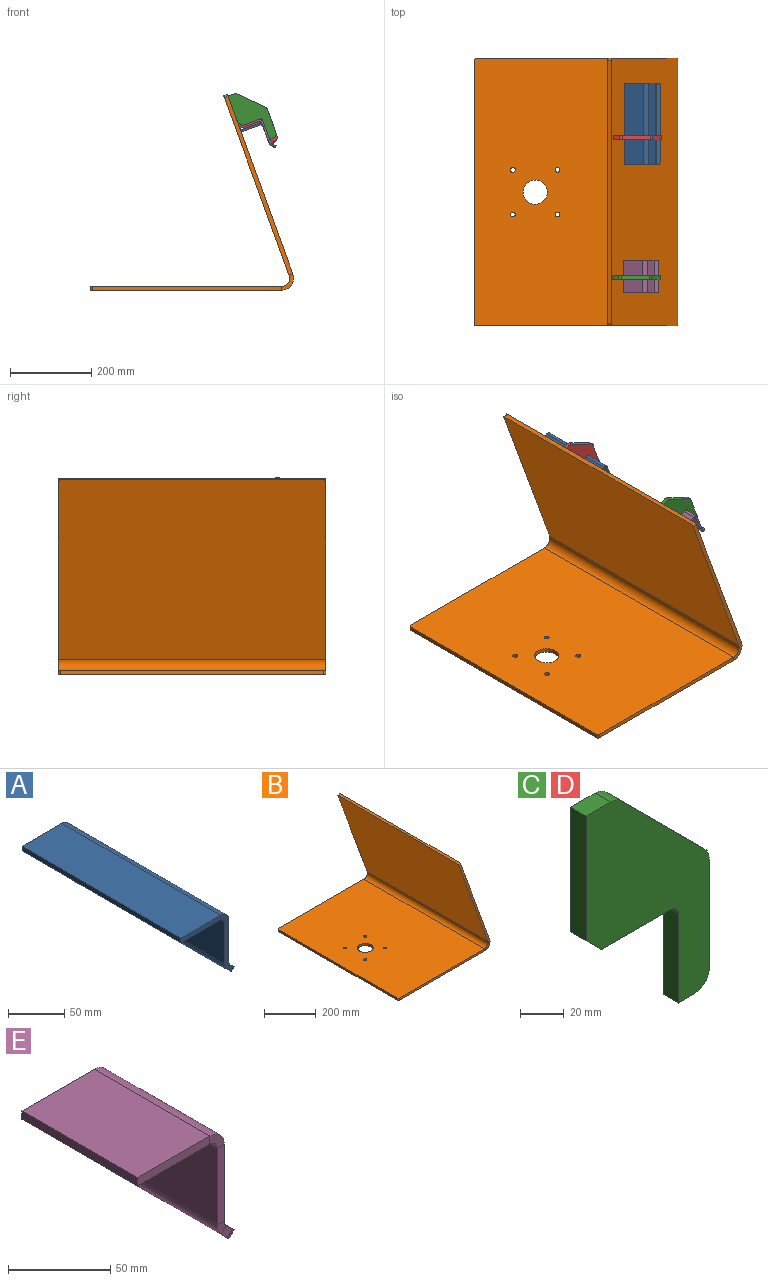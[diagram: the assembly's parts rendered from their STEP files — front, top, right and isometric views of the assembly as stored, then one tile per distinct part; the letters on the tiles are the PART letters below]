
ASSEMBLY  parts=5 mates=6
PART A: 24 faces, bbox 69.1x200x70.6 mm
  f0: plane 50x5mm, normal (0,1,0), area 250mm2, adj f2,f3,f4,f21
  f1: plane 50x5mm, normal (0,-1,0), area 250mm2, adj f2,f3,f4,f20
  f2: plane 200x5mm, normal (-1,0,0), area 1000mm2, adj f0,f1,f3,f4
  f3: plane 200x50mm, normal (0,0,-1), area 10000mm2, adj f0,f1,f2,f23
  f4: plane 200x50mm, normal (0,0,1), area 10000mm2, adj f0,f1,f2,f22
  f5: plane 45.86x5mm, normal (0,1,0), area 229.3mm2, adj f7,f8,f17,f21
  f6: plane 45.86x5mm, normal (0,-1,0), area 229.3mm2, adj f7,f8,f16,f20
  f7: plane 200x45.86mm, normal (-1,0,0), area 9171.6mm2, adj f5,f6,f18,f23
  f8: plane 200x45.86mm, normal (1,0,0), area 9171.6mm2, adj f5,f6,f19,f22
  f9: plane 7.68x7.68mm, normal (0,1,0), area 29.3mm2, adj f12,f13,f14,f17
  f10: plane 190x3.54mm, normal (0.71,0,-0.71), area 950mm2, adj f12,f13,f14,f15
  f11: plane 7.68x7.68mm, normal (0,-1,0), area 29.3mm2, adj f12,f13,f15,f16
  f12: plane 200x7.68mm, normal (-0.71,0,-0.71), area 2160.8mm2, adj f9,f10,f11,f14,f15,f18
  f13: plane 200x7.68mm, normal (0.71,0,0.71), area 2160.8mm2, adj f9,f10,f11,f14,f15,f19
  f14: cylinder r=5mm len=7.07mm, axis (-0.71,0,-0.71), area 39.3mm2, adj f9,f10,f12,f13
  f15: cylinder r=5mm len=7.07mm, axis (0.71,0,0.71), area 39.3mm2, adj f10,f11,f12,f13
  f16: plane 7.07x6.46mm, normal (0,-1,0), area 29.5mm2, adj f6,f11,f18,f19
  f17: plane 7.07x6.46mm, normal (0,1,0), area 29.5mm2, adj f5,f9,f18,f19
  f18: cylinder r=10mm len=200mm, axis (0,-1,0), area 1570.8mm2, adj f7,f12,f16,f17
  f19: cylinder r=5mm len=200mm, axis (0,-1,0), area 785.4mm2, adj f8,f13,f16,f17
  f20: plane 10x10mm, normal (0,-1,0), area 58.9mm2, adj f1,f6,f22,f23
  f21: plane 10x10mm, normal (0,1,0), area 58.9mm2, adj f0,f5,f22,f23
  f22: cylinder r=10mm len=200mm, axis (0,-1,0), area 3141.6mm2, adj f4,f8,f20,f21
  f23: cylinder r=5mm len=200mm, axis (0,-1,0), area 1570.8mm2, adj f3,f7,f20,f21
PART B: 23 faces, bbox 501.4x660x483.3 mm
  f0: plane 466.44x10mm, normal (0,1,0), area 4664.4mm2, adj f8,f9,f11,f20
  f1: plane 466.44x10mm, normal (0,-1,0), area 4664.4mm2, adj f8,f9,f10,f19
  f2: cylinder r=30mm len=60mm, axis (0,0,-1), area 1885mm2, adj f8,f9
  f3: cylinder r=6mm len=12mm, axis (0,0,-1), area 377mm2, adj f8,f9
  f4: cylinder r=6mm len=12mm, axis (0,0,-1), area 377mm2, adj f8,f9
  f5: cylinder r=6mm len=12mm, axis (0,0,-1), area 377mm2, adj f8,f9
  f6: cylinder r=6mm len=12mm, axis (0,0,-1), area 377mm2, adj f8,f9
  f7: plane 650x10mm, normal (-1,0,0), area 6500mm2, adj f8,f9,f10,f11
  f8: plane 660x471.44mm, normal (0,0,-1), area 307857.9mm2, adj f0,f1,f2,f3,f4,f5,f6,f7
  f9: plane 660x471.44mm, normal (0,0,1), area 307857.9mm2, adj f0,f1,f2,f3,f4,f5,f6,f7
  f10: cylinder r=5mm len=10mm, axis (0,0,-1), area 78.5mm2, adj f1,f7,f8,f9
  f11: cylinder r=5mm len=10mm, axis (0,0,1), area 78.5mm2, adj f0,f7,f8,f9
  f12: plane 441.73x168.93mm, normal (0,1,0), area 4664.4mm2, adj f15,f16,f17,f20
  f13: plane 650x9.4mm, normal (-0.34,0,0.94), area 6500mm2, adj f15,f16,f17,f18
  f14: plane 441.73x168.93mm, normal (0,-1,0), area 4664.4mm2, adj f15,f16,f18,f19
  f15: plane 660x443.01mm, normal (0.94,0,0.34), area 311137.7mm2, adj f12,f13,f14,f17,f18,f21
  f16: plane 660x443.01mm, normal (-0.94,0,-0.34), area 311137.7mm2, adj f12,f13,f14,f17,f18,f22
  f17: cylinder r=5mm len=11.11mm, axis (0.94,0,0.34), area 78.5mm2, adj f12,f13,f15,f16
  f18: cylinder r=5mm len=11.11mm, axis (-0.94,0,-0.34), area 78.5mm2, adj f13,f14,f15,f16
  f19: plane 40.26x30mm, normal (0,-1,0), area 480mm2, adj f1,f14,f21,f22
  f20: plane 40.26x30mm, normal (0,1,0), area 480mm2, adj f0,f12,f21,f22
  f21: cylinder r=30mm len=660mm, axis (0,-1,0), area 38013.3mm2, adj f8,f15,f19,f20
  f22: cylinder r=20mm len=660mm, axis (0,-1,0), area 25342.2mm2, adj f9,f16,f19,f20
PART C: 14 faces, bbox 80x10x135 mm
  f0: plane 70x10mm, normal (-1,0,0), area 700mm2, adj f6,f7,f8,f9
  f1: plane 45x10mm, normal (0,0,-1), area 450mm2, adj f7,f8,f9,f10
  f2: plane 50x10mm, normal (-1,0,0), area 500mm2, adj f3,f7,f8,f10
  f3: plane 10x10mm, normal (0,0,-1), area 100mm2, adj f2,f7,f8,f11
  f4: plane 60.86x10mm, normal (1,0,0), area 608.6mm2, adj f7,f8,f11,f12
  f5: plane 54.14x54.14mm, normal (0.71,0,0.71), area 765.7mm2, adj f7,f8,f12,f13
  f6: plane 15.86x10mm, normal (0,0,1), area 158.6mm2, adj f0,f7,f8,f13
  f7: plane 135x80mm, normal (0,-1,0), area 5629.6mm2, adj f0,f1,f2,f3,f4,f5,f6,f9
  f8: plane 135x80mm, normal (0,1,0), area 5629.6mm2, adj f0,f1,f2,f3,f4,f5,f6,f9
  f9: plane 10x10mm, normal (-0.71,0,-0.71), area 141.4mm2, adj f0,f1,f7,f8
  f10: cylinder r=5mm len=10mm, axis (0,-1,0), area 78.5mm2, adj f1,f2,f7,f8
  f11: cylinder r=10mm len=10mm, axis (0,1,0), area 157.1mm2, adj f3,f4,f7,f8
  f12: cylinder r=10mm len=10mm, axis (0,1,0), area 78.5mm2, adj f4,f5,f7,f8
  f13: cylinder r=10mm len=10mm, axis (0,1,0), area 78.5mm2, adj f5,f6,f7,f8
PART D: same geometry as C
PART E: 24 faces, bbox 69.1x80x70.6 mm
  f0: plane 50x5mm, normal (0,1,0), area 250mm2, adj f2,f3,f4,f21
  f1: plane 50x5mm, normal (0,-1,0), area 250mm2, adj f2,f3,f4,f20
  f2: plane 80x5mm, normal (-1,0,0), area 400mm2, adj f0,f1,f3,f4
  f3: plane 80x50mm, normal (0,0,-1), area 4000mm2, adj f0,f1,f2,f23
  f4: plane 80x50mm, normal (0,0,1), area 4000mm2, adj f0,f1,f2,f22
  f5: plane 45.86x5mm, normal (0,1,0), area 229.3mm2, adj f7,f8,f17,f21
  f6: plane 45.86x5mm, normal (0,-1,0), area 229.3mm2, adj f7,f8,f16,f20
  f7: plane 80x45.86mm, normal (-1,0,0), area 3668.6mm2, adj f5,f6,f18,f23
  f8: plane 80x45.86mm, normal (1,0,0), area 3668.6mm2, adj f5,f6,f19,f22
  f9: plane 7.68x7.68mm, normal (0,1,0), area 29.3mm2, adj f12,f13,f14,f17
  f10: plane 70x3.54mm, normal (0.71,0,-0.71), area 350mm2, adj f12,f13,f14,f15
  f11: plane 7.68x7.68mm, normal (0,-1,0), area 29.3mm2, adj f12,f13,f15,f16
  f12: plane 80x7.68mm, normal (-0.71,0,-0.71), area 857.9mm2, adj f9,f10,f11,f14,f15,f18
  f13: plane 80x7.68mm, normal (0.71,0,0.71), area 857.9mm2, adj f9,f10,f11,f14,f15,f19
  f14: cylinder r=5mm len=7.07mm, axis (-0.71,0,-0.71), area 39.3mm2, adj f9,f10,f12,f13
  f15: cylinder r=5mm len=7.07mm, axis (0.71,0,0.71), area 39.3mm2, adj f10,f11,f12,f13
  f16: plane 7.07x6.46mm, normal (0,-1,0), area 29.5mm2, adj f6,f11,f18,f19
  f17: plane 7.07x6.46mm, normal (0,1,0), area 29.5mm2, adj f5,f9,f18,f19
  f18: cylinder r=10mm len=80mm, axis (0,-1,0), area 628.3mm2, adj f7,f12,f16,f17
  f19: cylinder r=5mm len=80mm, axis (0,-1,0), area 314.2mm2, adj f8,f13,f16,f17
  f20: plane 10x10mm, normal (0,-1,0), area 58.9mm2, adj f1,f6,f22,f23
  f21: plane 10x10mm, normal (0,1,0), area 58.9mm2, adj f0,f5,f22,f23
  f22: cylinder r=10mm len=80mm, axis (0,-1,0), area 1256.6mm2, adj f4,f8,f20,f21
  f23: cylinder r=5mm len=80mm, axis (0,-1,0), area 628.3mm2, adj f3,f7,f20,f21
PLACE A rot(axis=(0,-1,0),20deg) t=(-90.43,167.7,394.64)mm
PLACE B t=(-14.1,0,-5.13)mm
PLACE C rot(axis=(0,-1,0),20deg) t=(-146.9,-206.5,388.99)mm
PLACE D rot(axis=(0,-1,0),20deg) t=(-143.82,138.5,380.53)mm
PLACE E rot(axis=(0,-1,0),20deg) t=(-93.51,-209,403.1)mm
MATE planar C.f1 <-> E.f4  axis (0.34,0,-0.94) through (-116.36,-211.5,400.1)mm
MATE planar E.f2 <-> B.f15  axis (-0.94,0,-0.34) through (-146.05,-209,386.64)mm
MATE planar C.f0 <-> B.f15  axis (-0.94,0,-0.34) through (-162.29,-211.5,431.28)mm
MATE planar D.f1 <-> A.f4  axis (0.34,0,-0.94) through (-113.28,133.5,391.65)mm
MATE planar D.f0 <-> B.f15  axis (-0.94,0,-0.34) through (-159.21,133.5,422.82)mm
MATE planar A.f2 <-> B.f15  axis (-0.94,0,-0.34) through (-142.97,167.7,378.18)mm
